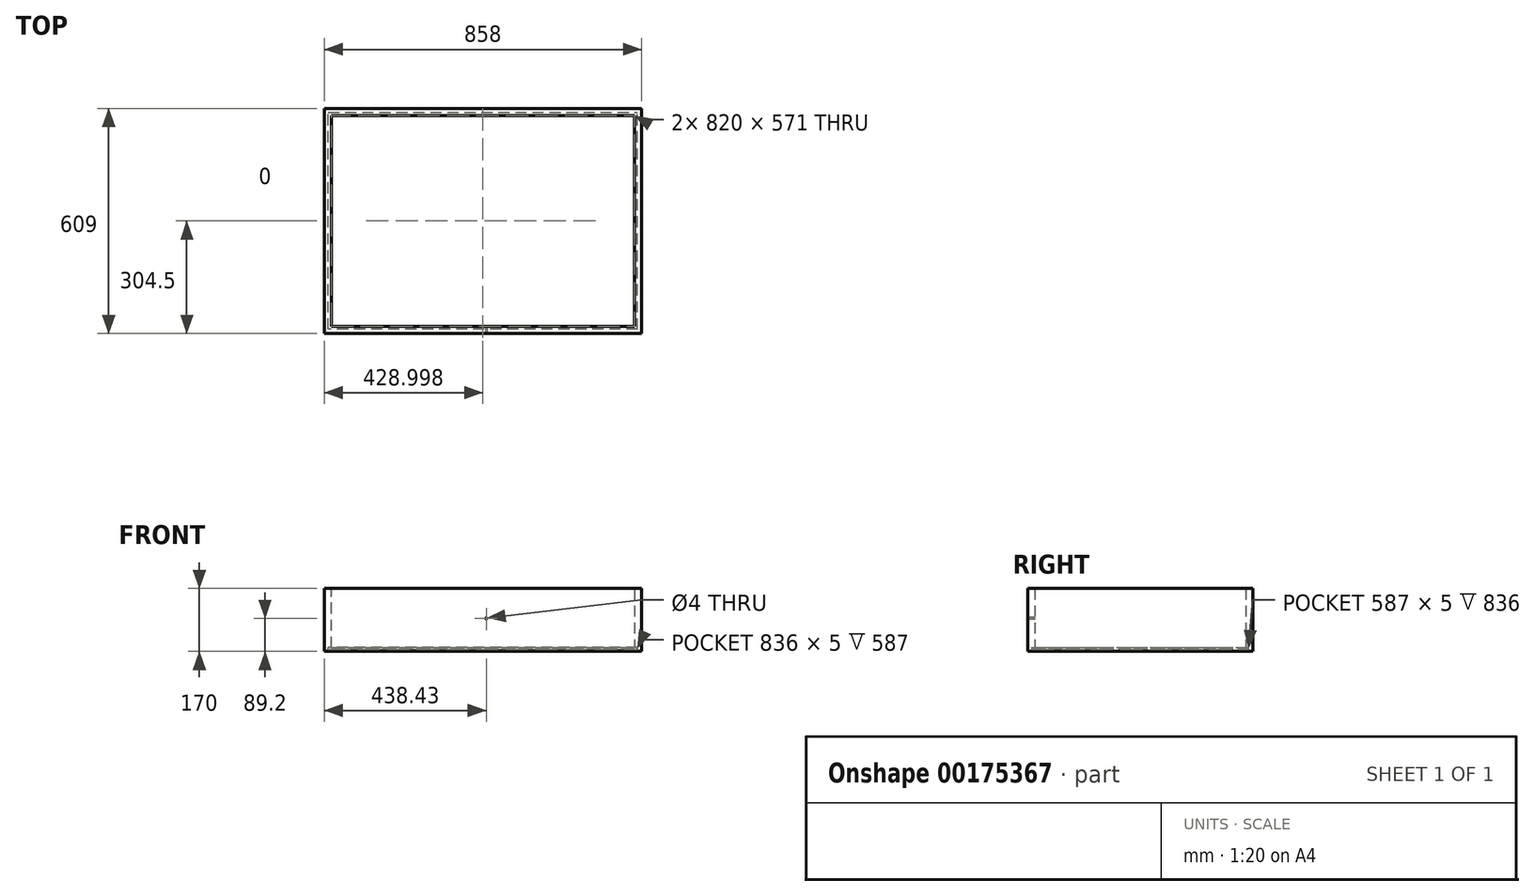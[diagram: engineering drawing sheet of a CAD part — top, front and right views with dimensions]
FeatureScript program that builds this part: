
annotation { "Feature Type Name" : "Feature", "Feature Type Description" : "" }
export const myFeature = defineFeature(function(context is Context, id is Id, definition is map)
    precondition{}
    {
        {
            var Q0;
            Q0=qCreatedBy(makeId("Front.planeOp"),FACE);
            var sketch = newSketch(context, id + "F0", { "sketchPlane" : qUnion([Q0])});
            skLineSegment(sketch, "E0.bottom", {"start": v(-438.43, 80.8) * mm, "end": v(419.57, 80.8) * mm});
            skLineSegment(sketch, "E0.top", {"start": v(-438.43, -89.2) * mm, "end": v(419.57, -89.2) * mm});
            skLineSegment(sketch, "E0.left", {"start": v(-438.43, 80.8) * mm, "end": v(-438.43, -89.2) * mm});
            skLineSegment(sketch, "E0.right", {"start": v(419.57, 80.8) * mm, "end": v(419.57, -89.2) * mm});
            skSolve(sketch);
        }
        {
            var Q0;
            Q0=makeQuery(id+"F0.imprint","IMPRINT",FACE,{"disambiguationData":[TD([[makeQuery(id+"F0.imprint","IMPRINT",EDGE,{"derivedFrom":sQuery(id+"F0.wireOp",EDGE,"E0.bottom")}),-1.0]])]});
            extrude(context, id + "F1", {"entities" : qUnion([Q0]), "depth" : 19 * mm});
        }
        {
            var Q0;
            Q0=makeQuery(id+"F1.opExtrude","CAP_FACE",FACE,{"disambiguationData":[OSD([sQuery(id+"F0.wireOp",EDGE,"E0.bottom"),sQuery(id+"F0.wireOp",EDGE,"E0.top"),sQuery(id+"F0.wireOp",EDGE,"E0.left"),sQuery(id+"F0.wireOp",EDGE,"E0.right")])],"isStart":true});
            var sketch = newSketch(context, id + "F2", { "sketchPlane" : qUnion([Q0])});
            skLineSegment(sketch, "E1.bottom", {"start": v(-419.57, 80.8) * mm, "end": v(-400.57, 80.8) * mm});
            skLineSegment(sketch, "E1.top", {"start": v(-419.57, -89.2) * mm, "end": v(-400.57, -89.2) * mm});
            skLineSegment(sketch, "E1.left", {"start": v(-419.57, 80.8) * mm, "end": v(-419.57, -89.2) * mm});
            skLineSegment(sketch, "E1.right", {"start": v(-400.57, 80.8) * mm, "end": v(-400.57, -89.2) * mm});
            skLineSegment(sketch, "E2.bottom", {"start": v(438.43, 80.8) * mm, "end": v(419.43, 80.8) * mm});
            skLineSegment(sketch, "E2.top", {"start": v(438.43, -89.2) * mm, "end": v(419.43, -89.2) * mm});
            skLineSegment(sketch, "E2.left", {"start": v(438.43, 80.8) * mm, "end": v(438.43, -89.2) * mm});
            skLineSegment(sketch, "E2.right", {"start": v(419.43, 80.8) * mm, "end": v(419.43, -89.2) * mm});
            skSolve(sketch);
        }
        {
            var Q0;
            Q0=makeQuery(id+"F2.imprint","IMPRINT",FACE,{"disambiguationData":[TD([[makeQuery(id+"F2.imprint","IMPRINT",EDGE,{"derivedFrom":sQuery(id+"F2.wireOp",EDGE,"E1.bottom")}),1.0]])]});
            var Q1;
            Q1=makeQuery(id+"F2.imprint","IMPRINT",FACE,{"disambiguationData":[TD([[makeQuery(id+"F2.imprint","IMPRINT",EDGE,{"derivedFrom":sQuery(id+"F2.wireOp",EDGE,"E2.bottom")}),1.0]])]});
            extrude(context, id + "F3", {"entities" : qUnion([Q0, Q1]), "operationType" : NewBodyOperationType.ADD, "depth" : 590 * mm});
        }
        {
            var Q0;
            Q0=makeQuery(id+"F3.opExtrude","SWEPT_FACE",FACE,{"disambiguationData":[OSD([sQuery(id+"F2.wireOp",EDGE,"E1.right")])]});
            var sketch = newSketch(context, id + "F4", { "sketchPlane" : qUnion([Q0])});
            skLineSegment(sketch, "E3.bottom", {"start": v(-590, 80.8) * mm, "end": v(-571, 80.8) * mm});
            skLineSegment(sketch, "E3.top", {"start": v(-590, -89.2) * mm, "end": v(-571, -89.2) * mm});
            skLineSegment(sketch, "E3.left", {"start": v(-590, 80.8) * mm, "end": v(-590, -89.2) * mm});
            skLineSegment(sketch, "E3.right", {"start": v(-571, 80.8) * mm, "end": v(-571, -89.2) * mm});
            skSolve(sketch);
        }
        {
            var Q0;
            Q0=makeQuery(id+"F4.imprint","IMPRINT",FACE,{"disambiguationData":[TD([[makeQuery(id+"F4.imprint","IMPRINT",EDGE,{"derivedFrom":sQuery(id+"F4.wireOp",EDGE,"E3.bottom")}),-1.0]])]});
            extrude(context, id + "F5", {"entities" : qUnion([Q0]), "operationType" : NewBodyOperationType.ADD, "depth" : 824 * mm});
        }
        {
            var Q0;
            Q0=makeQuery(id+"F5.opExtrude","SWEPT_FACE",FACE,{"disambiguationData":[OSD([sQuery(id+"F4.wireOp",EDGE,"E3.right")])]});
            var sketch = newSketch(context, id + "F6", { "sketchPlane" : qUnion([Q0])});
            skLineSegment(sketch, "E4.bottom", {"start": v(-419.43, -79.2) * mm, "end": v(400.57, -79.2) * mm});
            skLineSegment(sketch, "E4.top", {"start": v(-419.43, -84.2) * mm, "end": v(400.57, -84.2) * mm});
            skLineSegment(sketch, "E4.left", {"start": v(-419.43, -79.2) * mm, "end": v(-419.43, -84.2) * mm});
            skLineSegment(sketch, "E4.right", {"start": v(400.57, -79.2) * mm, "end": v(400.57, -84.2) * mm});
            skSolve(sketch);
        }
        {
            var Q0;
            Q0=makeQuery(id+"F6.imprint","IMPRINT",FACE,{"disambiguationData":[TD([[makeQuery(id+"F6.imprint","IMPRINT",EDGE,{"derivedFrom":sQuery(id+"F6.wireOp",EDGE,"E4.bottom")}),-1.0]])]});
            extrude(context, id + "F7", {"entities" : qUnion([Q0]), "operationType" : NewBodyOperationType.REMOVE, "oppositeDirection" : true, "depth" : 8 * mm});
        }
        {
            var Q0;
            Q0=makeQuery(id+"Fq09jqGDxv2tgTj_1.boolean.opBoolean","MERGE",FACE,{"derivedFrom":[makeQuery(id+"F1.opExtrude","CAP_FACE",FACE,{"disambiguationData":[OSD([sQuery(id+"F0.wireOp",EDGE,"E0.bottom"),sQuery(id+"F0.wireOp",EDGE,"E0.top"),sQuery(id+"F0.wireOp",EDGE,"E0.left"),sQuery(id+"F0.wireOp",EDGE,"E0.right")])],"isStart":true}),makeQuery(id+"Fq09jqGDxv2tgTj_1.opExtrude","SWEPT_FACE",FACE,{"disambiguationData":[OSD([sQuery(id+"FyuLYs5OEGR4514_1.wireOp",EDGE,"adbQdK2Q-yDR9-2hoD-vhQC-gtOX9KH7EAfe.right")])]})]});
            var sketch = newSketch(context, id + "F8", { "sketchPlane" : qUnion([Q0])});
            skLineSegment(sketch, "E5.bottom", {"start": v(-400.57, -79.2) * mm, "end": v(419.43, -79.2) * mm});
            skLineSegment(sketch, "E5.top", {"start": v(-400.57, -84.2) * mm, "end": v(419.43, -84.2) * mm});
            skLineSegment(sketch, "E5.left", {"start": v(-400.57, -79.2) * mm, "end": v(-400.57, -84.2) * mm});
            skLineSegment(sketch, "E5.right", {"start": v(419.43, -79.2) * mm, "end": v(419.43, -84.2) * mm});
            skSolve(sketch);
        }
        {
            var Q0;
            Q0=makeQuery(id+"F8.imprint","IMPRINT",FACE,{"disambiguationData":[TD([[makeQuery(id+"F8.imprint","IMPRINT",EDGE,{"derivedFrom":sQuery(id+"F8.wireOp",EDGE,"E5.bottom")}),-1.0]])]});
            extrude(context, id + "F9", {"entities" : qUnion([Q0]), "operationType" : NewBodyOperationType.REMOVE, "oppositeDirection" : true, "depth" : 8 * mm});
        }
        {
            var Q0;
            Q0=makeQuery(id+"F9.boolean.opBoolean","MERGE",FACE,{"derivedFrom":[makeQuery(id+"F7.boolean.opBoolean","MERGE",FACE,{"derivedFrom":[makeQuery(id+"F3.opExtrude","SWEPT_FACE",FACE,{"disambiguationData":[OSD([sQuery(id+"F2.wireOp",EDGE,"E2.right")])]}),makeQuery(id+"F7.opExtrude","SWEPT_FACE",FACE,{"disambiguationData":[OSD([sQuery(id+"F6.wireOp",EDGE,"E4.left")])]})]}),makeQuery(id+"F9.opExtrude","SWEPT_FACE",FACE,{"disambiguationData":[OSD([sQuery(id+"F8.wireOp",EDGE,"E5.right")])]})]});
            var sketch = newSketch(context, id + "F10", { "sketchPlane" : qUnion([Q0])});
            skLineSegment(sketch, "E6.bottom", {"start": v(-8, -79.2) * mm, "end": v(579, -79.2) * mm});
            skLineSegment(sketch, "E6.top", {"start": v(-8, -84.2) * mm, "end": v(579, -84.2) * mm});
            skLineSegment(sketch, "E6.left", {"start": v(-8, -79.2) * mm, "end": v(-8, -84.2) * mm});
            skLineSegment(sketch, "E6.right", {"start": v(579, -79.2) * mm, "end": v(579, -84.2) * mm});
            skSolve(sketch);
        }
        {
            var Q0;
            {var subQ25=sQuery(id+"F10.wireOp",EDGE,"E6.left");Q0=makeQuery(id+"F10.imprint","IMPRINT",FACE,{"disambiguationData":[TD([[makeQuery(id+"F10.imprint","IMPRINT",EDGE,{"derivedFrom":subQ25}),1.0]])]});}
            extrude(context, id + "F11", {"entities" : qUnion([Q0]), "operationType" : NewBodyOperationType.REMOVE, "oppositeDirection" : true, "depth" : 8 * mm});
        }
        {
            var Q0;
            Q0=makeQuery(id+"F9.boolean.opBoolean","MERGE",FACE,{"derivedFrom":[makeQuery(id+"F7.boolean.opBoolean","MERGE",FACE,{"derivedFrom":[makeQuery(id+"F3.opExtrude","SWEPT_FACE",FACE,{"disambiguationData":[OSD([sQuery(id+"F2.wireOp",EDGE,"E1.right")])]}),makeQuery(id+"F7.opExtrude","SWEPT_FACE",FACE,{"disambiguationData":[OSD([sQuery(id+"F6.wireOp",EDGE,"E4.right")])]})]}),makeQuery(id+"F9.opExtrude","SWEPT_FACE",FACE,{"disambiguationData":[OSD([sQuery(id+"F8.wireOp",EDGE,"E5.left")])]})]});
            var sketch = newSketch(context, id + "F12", { "sketchPlane" : qUnion([Q0])});
            skLineSegment(sketch, "E7.bottom", {"start": v(8, -79.2) * mm, "end": v(-579, -79.2) * mm});
            skLineSegment(sketch, "E7.top", {"start": v(8, -84.2) * mm, "end": v(-579, -84.2) * mm});
            skLineSegment(sketch, "E7.left", {"start": v(8, -79.2) * mm, "end": v(8, -84.2) * mm});
            skLineSegment(sketch, "E7.right", {"start": v(-579, -79.2) * mm, "end": v(-579, -84.2) * mm});
            skSolve(sketch);
        }
        {
            var Q0;
            {var subQ25=sQuery(id+"F12.wireOp",EDGE,"E7.left");Q0=makeQuery(id+"F12.imprint","IMPRINT",FACE,{"disambiguationData":[TD([[makeQuery(id+"F12.imprint","IMPRINT",EDGE,{"derivedFrom":subQ25}),-1.0]])]});}
            extrude(context, id + "F13", {"entities" : qUnion([Q0]), "operationType" : NewBodyOperationType.REMOVE, "oppositeDirection" : true, "depth" : 8 * mm});
        }
        {
            var Q0;
            Q0=makeQuery(id+"F1.opExtrude","CAP_FACE",FACE,{"disambiguationData":[OSD([sQuery(id+"F0.wireOp",EDGE,"E0.bottom"),sQuery(id+"F0.wireOp",EDGE,"E0.top"),sQuery(id+"F0.wireOp",EDGE,"E0.left"),sQuery(id+"F0.wireOp",EDGE,"E0.right")])],"isStart":false});
            var sketch = newSketch(context, id + "F14", { "sketchPlane" : qUnion([Q0])});
            skCircle(sketch, "E8", {"center": v(0, 0) * mm, "radius": 2 * mm});
            skSolve(sketch);
        }
        {
            var Q0;
            Q0 = qSketchRegion(id + "F14", true);
            extrude(context, id + "F15", {"entities" : qUnion([Q0]), "operationType" : NewBodyOperationType.REMOVE, "oppositeDirection" : true, "depth" : 19 * mm});
        }
    });
